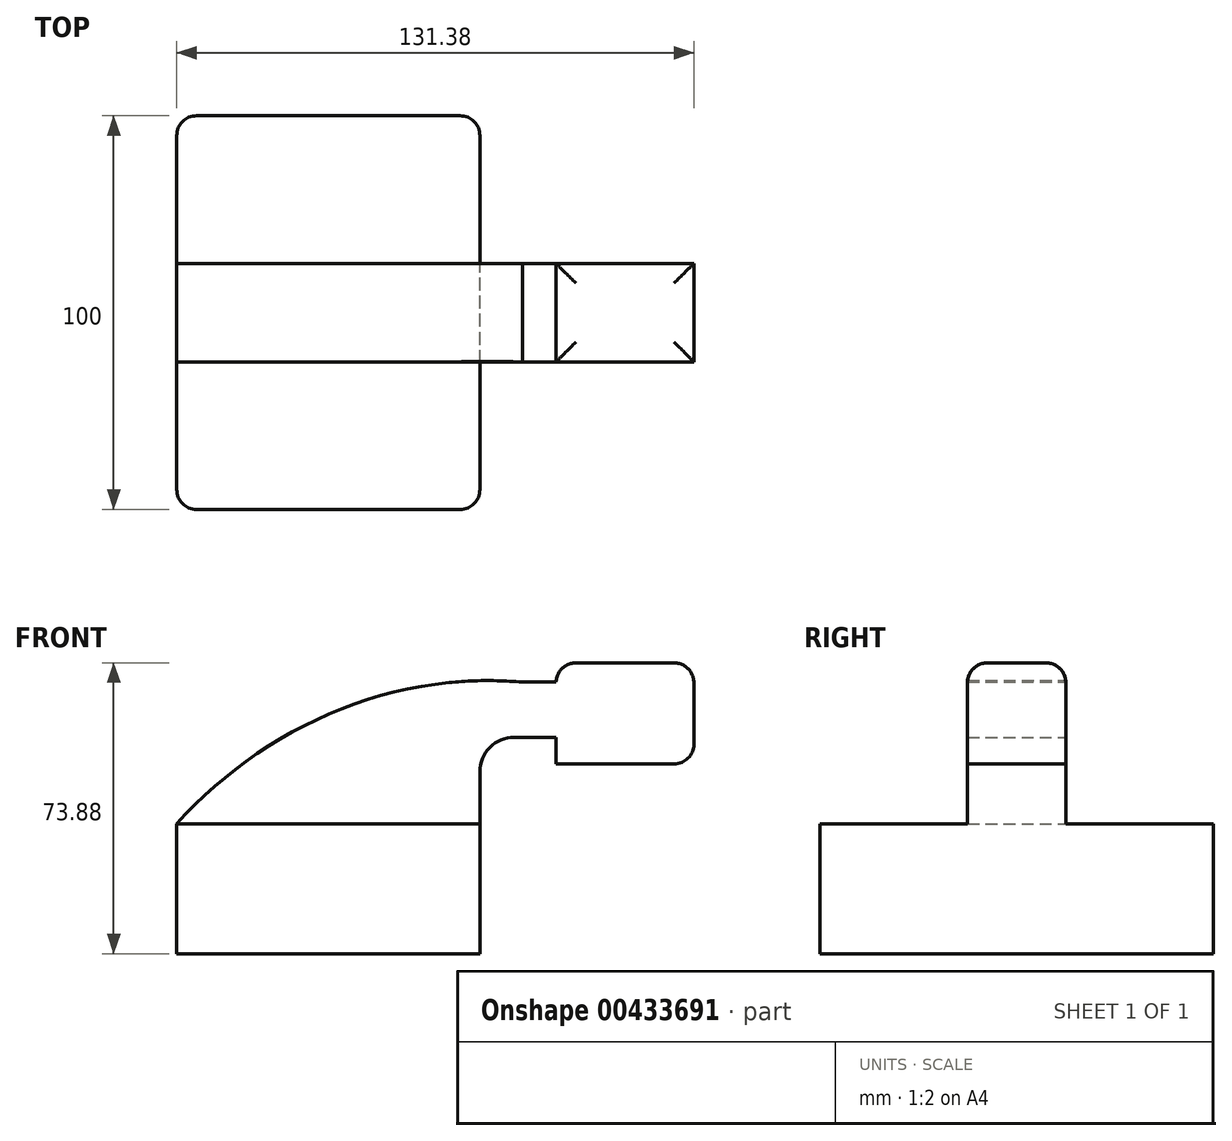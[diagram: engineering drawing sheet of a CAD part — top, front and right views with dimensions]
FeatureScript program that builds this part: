
annotation { "Feature Type Name" : "Feature", "Feature Type Description" : "" }
export const myFeature = defineFeature(function(context is Context, id is Id, definition is map)
    precondition{}
    {
        {
            var Q0;
            Q0=qCreatedBy(makeId("Front.planeOp"),FACE);
            var sketch = newSketch(context, id + "F0", { "sketchPlane" : qUnion([Q0])});
            skLineSegment(sketch, "E0.bottom", {"start": v(30.5, -11.01) * mm, "end": v(-46.5, -11.01) * mm});
            skLineSegment(sketch, "E0.top", {"start": v(30.5, 21.99) * mm, "end": v(-46.5, 21.99) * mm});
            skLineSegment(sketch, "E0.left", {"start": v(30.5, -11.01) * mm, "end": v(30.5, 21.99) * mm});
            skLineSegment(sketch, "E0.right", {"start": v(-46.5, -11.01) * mm, "end": v(-46.5, 21.99) * mm});
            skPoint(sketch, "E0.middle", {"position": v(-8, 5.49) * mm});
            skLineSegment(sketch, "E1.bottom", {"start": v(84.87, 37.2) * mm, "end": v(49.87, 37.2) * mm});
            skLineSegment(sketch, "E1.top", {"start": v(84.87, 62.87) * mm, "end": v(49.87, 62.87) * mm});
            skLineSegment(sketch, "E1.left", {"start": v(84.87, 37.2) * mm, "end": v(84.87, 62.87) * mm});
            skLineSegment(sketch, "E1.right", {"start": v(49.87, 37.2) * mm, "end": v(49.87, 62.87) * mm});
            skPoint(sketch, "E1.middle", {"position": v(67.37, 50.03) * mm});
            skLineSegment(sketch, "E2", {"start": v(30.5, 21.99) * mm, "end": v(30.5, 35.18) * mm});
            skArc(sketch, "E3", {"start": v(30.5, 35.18) * mm, "mid": v(33.07, 41.4) * mm, "end": v(39.3, 43.99) * mm});
            skLineSegment(sketch, "E4", {"start": v(39.3, 43.99) * mm, "end": v(65.62, 43.99) * mm});
            skLineSegment(sketch, "E5.0", {"start": v(39.3, 57.99) * mm, "end": v(65.62, 57.99) * mm});
            skArc(sketch, "E5.1", {"start": v(16.5, 35.18) * mm, "mid": v(23.17, 51.3) * mm, "end": v(39.3, 57.99) * mm});
            skLineSegment(sketch, "E5.2", {"start": v(16.5, 21.99) * mm, "end": v(16.5, 35.18) * mm});
            skFitSpline(sketch, "E6", {"points": [v(-46.5, 21.99) * mm, v(41.3, 57.99) * mm], "startDerivative": vector(63.04, 70.56) * mm, "endDerivative": vector(103.25, -9.21) * mm});
            skSolve(sketch);
        }
        {
            var Q0;
            Q0=makeQuery(id+"F0.imprint","IMPRINT",FACE,{"disambiguationData":[TD([[makeQuery(id+"F0.imprint","IMPRINT",EDGE,{"derivedFrom":sQuery(id+"F0.wireOp",EDGE,"E0.bottom")}),-1.0]])]});
            extrude(context, id + "F1", {"entities" : qUnion([Q0]), "endBound" : BoundingType.SYMMETRIC, "depth" : 100 * mm});
        }
        {
            var Q0;
            Q0 = qSketchRegion(id + "F0", true);
            extrude(context, id + "F2", {"entities" : qUnion([Q0]), "operationType" : NewBodyOperationType.ADD, "endBound" : BoundingType.SYMMETRIC, "depth" : 25 * mm});
        }
        {
            var Q0;
            Q0=makeQuery(id+"F2.opExtrude","SWEPT_FACE",FACE,{"disambiguationData":[OSD([sQuery(id+"F0.wireOp",EDGE,"E1.top")])]});
            var Q1;
            Q1=makeQuery(id+"F1.opExtrude","CAP_EDGE",EDGE,{"disambiguationData":[OSD([sQuery(id+"F0.wireOp",EDGE,"E0.left")])],"isStart":false});
            var Q2;
            Q2=makeQuery(id+"F1.opExtrude","CAP_EDGE",EDGE,{"disambiguationData":[OSD([sQuery(id+"F0.wireOp",EDGE,"E0.right")])],"isStart":false});
            var Q3;
            Q3=makeQuery(id+"F1.opExtrude","CAP_EDGE",EDGE,{"disambiguationData":[OSD([sQuery(id+"F0.wireOp",EDGE,"E0.left")])],"isStart":true});
            var Q4;
            Q4=makeQuery(id+"F2.opExtrude","SWEPT_EDGE",EDGE,{"disambiguationData":[OSD([sQuery(id+"F0.wireOp",EDGE,"E1.bottom"),sQuery(id+"F0.wireOp",EDGE,"E1.left")])]});
            fillet(context, id + "F3", {"entities" : qUnion([Q0, Q1, Q2, Q3, Q4]), "radius" : 5 * mm, "tangentPropagation" : true, "allowEdgeOverflow" : false});
        }
        {
            var Q0;
            Q0=makeQuery(id+"F1.opExtrude","CAP_EDGE",EDGE,{"disambiguationData":[OSD([sQuery(id+"F0.wireOp",EDGE,"E0.right")])],"isStart":true});
            fillet(context, id + "F4", {"entities" : qUnion([Q0]), "radius" : 5 * mm, "tangentPropagation" : true, "allowEdgeOverflow" : false});
        }
    });
